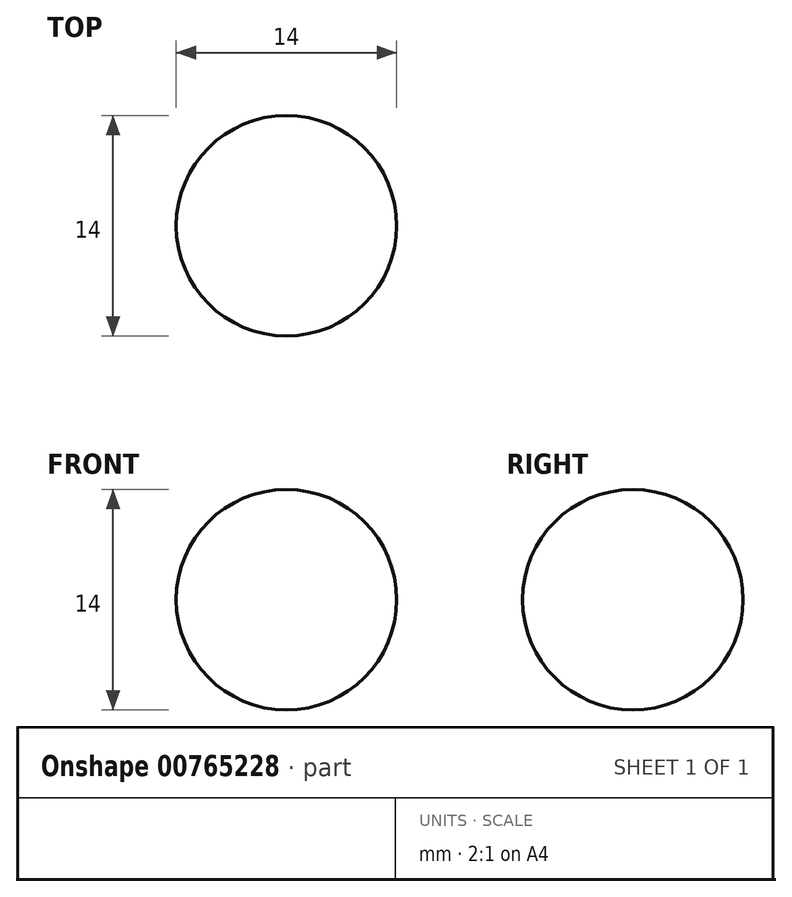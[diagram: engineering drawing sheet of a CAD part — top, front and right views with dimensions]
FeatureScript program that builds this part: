
annotation { "Feature Type Name" : "Feature", "Feature Type Description" : "" }
export const myFeature = defineFeature(function(context is Context, id is Id, definition is map)
    precondition{}
    {
        {
            var Q0;
            Q0=qCreatedBy(makeId("Front.planeOp"),FACE);
            var sketch = newSketch(context, id + "F0", { "sketchPlane" : qUnion([Q0])});
            skLineSegment(sketch, "E0", {"start": v(0, 0) * mm, "end": v(0, 14) * mm});
            skArc(sketch, "E1", {"start": v(0, 0) * mm, "mid": v(7, 7) * mm, "end": v(0, 14) * mm});
            skSolve(sketch);
        }
        {
            var Q0;
            Q0 = qSketchRegion(id + "F0", true);
            var Q1;
            Q1=sQuery(id+"F0.wireOp",EDGE,"E0");
            revolve(context, id + "F1", {"surfaceOperationType" : NewSurfaceOperationType.NEW, "entities" : qUnion([Q0]), "axis" : qUnion([Q1]), "revolveType" : RevolveType.FULL});
        }
    });
